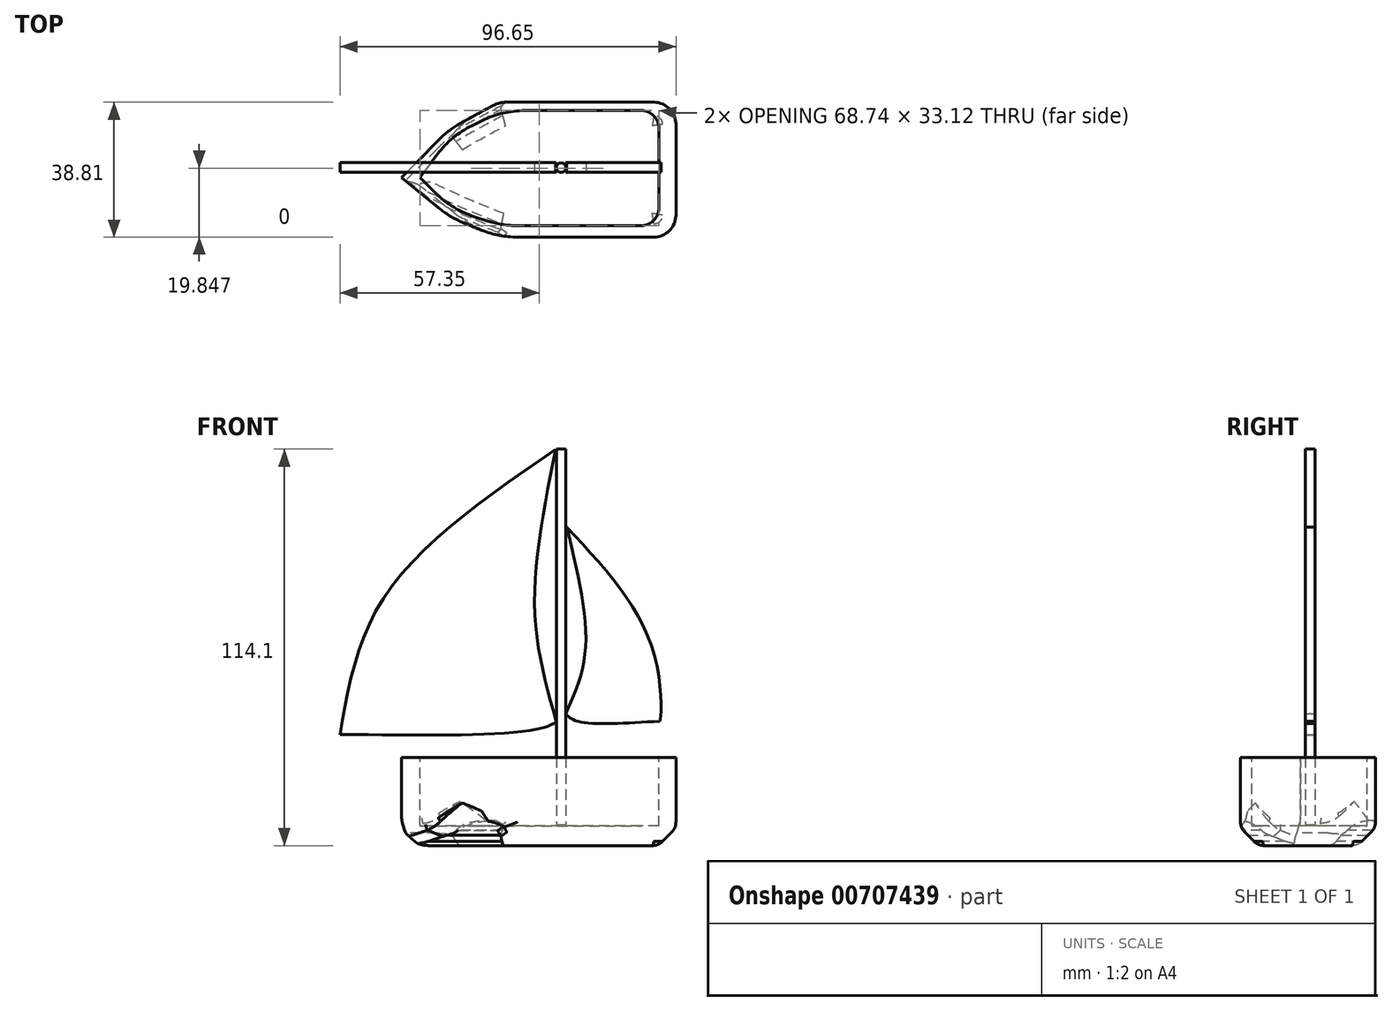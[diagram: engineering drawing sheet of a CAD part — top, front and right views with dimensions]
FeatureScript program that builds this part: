
annotation { "Feature Type Name" : "Feature", "Feature Type Description" : "" }
export const myFeature = defineFeature(function(context is Context, id is Id, definition is map)
    precondition{}
    {
        {
            var Q0;
            Q0=qCreatedBy(makeId("Top.planeOp"),FACE);
            var sketch = newSketch(context, id + "F0", { "sketchPlane" : qUnion([Q0])});
            skLineSegment(sketch, "E0", {"start": v(-20.58, 21.63) * mm, "end": v(23.87, 21.63) * mm});
            skLineSegment(sketch, "E1", {"start": v(-20.58, -17.18) * mm, "end": v(23.87, -17.18) * mm});
            skFitSpline(sketch, "E2", {"points": [v(-20.58, 21.63) * mm, v(-48.67, 0) * mm, v(-20.58, -17.18) * mm], "startDerivative": vector(-83.76, -44.37) * mm, "endDerivative": vector(84.8, -33.18) * mm});
            skLineSegment(sketch, "E3", {"start": v(-35.15, -11.18) * mm, "end": v(-48.67, 0) * mm});
            skLineSegment(sketch, "E4", {"start": v(-35.48, 13.4) * mm, "end": v(-48.67, 0) * mm});
            skLineSegment(sketch, "E5", {"start": v(30.22, 15.28) * mm, "end": v(30.22, -10.83) * mm});
            skPoint(sketch, "E6.visualSharp", {"position": v(30.22, 21.63) * mm});
            skArc(sketch, "E6.filletArc", {"start": v(30.22, 15.28) * mm, "mid": v(28.36, 19.77) * mm, "end": v(23.87, 21.63) * mm});
            skPoint(sketch, "E7.visualSharp", {"position": v(30.22, -17.18) * mm});
            skArc(sketch, "E7.filletArc", {"start": v(23.87, -17.18) * mm, "mid": v(28.36, -15.32) * mm, "end": v(30.22, -10.83) * mm});
            skSolve(sketch);
        }
        {
            var Q0;
            Q0=makeQuery(id+"F0.imprint","IMPRINT",FACE,{"disambiguationData":[TD([[makeQuery(id+"F0.imprint","IMPRINT",EDGE,{"derivedFrom":sQuery(id+"F0.wireOp",EDGE,"E0")}),-1.0]])]});
            extrude(context, id + "F1", {"entities" : qUnion([Q0]), "depth" : 25.4 * mm, "offsetDistance" : 25.4 * mm});
        }
        {
            var Q0;
            Q0=makeQuery(id+"F1.opExtrude","CAP_EDGE",EDGE,{"disambiguationData":[OSD([sQuery(id+"F0.wireOp",EDGE,"E2")])],"isStart":true});
            var Q1;
            Q1=makeQuery(id+"F1.opExtrude","CAP_EDGE",EDGE,{"disambiguationData":[OSD([sQuery(id+"F0.wireOp",EDGE,"E1")])],"isStart":true});
            var Q2;
            Q2=makeQuery(id+"F1.opExtrude","CAP_EDGE",EDGE,{"disambiguationData":[OSD([sQuery(id+"F0.wireOp",EDGE,"E4")])],"isStart":true});
            chamfer(context, id + "F2", {"entities" : qUnion([Q0, Q1, Q2]), "width" : 5.08 * mm, "tangentPropagation" : true});
        }
        {
            var Q0;
            Q0=makeQuery(id+"F2.opChamfer","BLEND_EDGE",EDGE,{"blendedFrom":[makeQuery(id+"F1.opExtrude","CAP_EDGE",EDGE,{"disambiguationData":[OSD([sQuery(id+"F0.wireOp",EDGE,"E2")])],"isStart":true}),makeQuery(id+"F1.opExtrude","SWEPT_FACE",FACE,{"disambiguationData":[OSD([sQuery(id+"F0.wireOp",EDGE,"E3")])]})],"blendedInto":[makeQuery(id+"F1.opExtrude","SWEPT_FACE",FACE,{"disambiguationData":[OSD([sQuery(id+"F0.wireOp",EDGE,"E3")])]})]});
            var Q1;
            {var subQ0=sQuery(id+"F0.wireOp",EDGE,"E4");Q1=makeQuery(id+"F2.opChamfer","BLEND_EDGE",EDGE,{"blendedFrom":[makeQuery(id+"F1.opExtrude","CAP_EDGE",EDGE,{"disambiguationData":[OSD([subQ0])],"isStart":true}),makeQuery(id+"F1.opExtrude","SWEPT_FACE",FACE,{"disambiguationData":[OSD([subQ0])]})],"blendedInto":[makeQuery(id+"F1.opExtrude","SWEPT_FACE",FACE,{"disambiguationData":[OSD([subQ0])]})]});}
            var Q2;
            {var subQ0=sQuery(id+"F0.wireOp",EDGE,"E2");Q2=makeQuery(id+"F2.opChamfer","BLEND_EDGE",EDGE,{"blendedFrom":[makeQuery(id+"F1.opExtrude","CAP_EDGE",EDGE,{"disambiguationData":[OSD([subQ0])],"isStart":true}),makeQuery(id+"F1.opExtrude","SWEPT_FACE",FACE,{"disambiguationData":[OSD([subQ0])]})],"blendedInto":[makeQuery(id+"F1.opExtrude","SWEPT_FACE",FACE,{"disambiguationData":[OSD([subQ0])]})]});}
            var Q3;
            Q3=makeQuery(id+"F2.opChamfer","BLEND_EDGE",EDGE,{"blendedFrom":[makeQuery(id+"F1.opExtrude","CAP_EDGE",EDGE,{"disambiguationData":[OSD([sQuery(id+"F0.wireOp",EDGE,"E4")])],"isStart":true}),makeQuery(id+"F1.opExtrude","SWEPT_FACE",FACE,{"disambiguationData":[OSD([sQuery(id+"F0.wireOp",EDGE,"E2")])]})],"blendedInto":[makeQuery(id+"F1.opExtrude","SWEPT_FACE",FACE,{"disambiguationData":[OSD([sQuery(id+"F0.wireOp",EDGE,"E2")])]})]});
            chamfer(context, id + "F3", {"entities" : qUnion([Q0, Q1, Q2, Q3]), "width" : 5.08 * mm, "tangentPropagation" : true});
        }
        {
            var Q0;
            {var subQ0=sQuery(id+"F0.wireOp",EDGE,"E2");Q0=makeQuery(id+"F3.opChamfer","BLEND_EDGE",EDGE,{"blendedFrom":[makeQuery(id+"F2.opChamfer","BLEND_EDGE",EDGE,{"blendedFrom":[makeQuery(id+"F1.opExtrude","CAP_EDGE",EDGE,{"disambiguationData":[OSD([subQ0])],"isStart":true}),makeQuery(id+"F1.opExtrude","SWEPT_FACE",FACE,{"disambiguationData":[OSD([subQ0])]})],"blendedInto":[makeQuery(id+"F1.opExtrude","SWEPT_FACE",FACE,{"disambiguationData":[OSD([subQ0])]})]}),makeQuery(id+"F2.opChamfer","BLEND_FACE",FACE,{"disambiguationData":[OSD([subQ0])]})],"blendedInto":[makeQuery(id+"F2.opChamfer","BLEND_FACE",FACE,{"disambiguationData":[OSD([subQ0])]})]});}
            var Q1;
            {var subQ0=sQuery(id+"F0.wireOp",EDGE,"E2");Q1=makeQuery(id+"F3.opChamfer","BLEND_EDGE",EDGE,{"blendedFrom":[makeQuery(id+"F2.opChamfer","BLEND_EDGE",EDGE,{"blendedFrom":[makeQuery(id+"F1.opExtrude","CAP_EDGE",EDGE,{"disambiguationData":[OSD([subQ0])],"isStart":true}),makeQuery(id+"F1.opExtrude","SWEPT_FACE",FACE,{"disambiguationData":[OSD([subQ0])]})],"blendedInto":[makeQuery(id+"F1.opExtrude","SWEPT_FACE",FACE,{"disambiguationData":[OSD([subQ0])]})]}),makeQuery(id+"F2.opChamfer","BLEND_FACE",FACE,{"disambiguationData":[OSD([sQuery(id+"F0.wireOp",EDGE,"E1")])]})],"blendedInto":[makeQuery(id+"F2.opChamfer","BLEND_FACE",FACE,{"disambiguationData":[OSD([sQuery(id+"F0.wireOp",EDGE,"E1")])]})]});}
            var Q2;
            {var subQ0=sQuery(id+"F0.wireOp",EDGE,"E1");Q2=makeQuery(id+"F2.opChamfer","BLEND_EDGE",EDGE,{"blendedFrom":[makeQuery(id+"F1.opExtrude","CAP_EDGE",EDGE,{"disambiguationData":[OSD([subQ0])],"isStart":true}),makeQuery(id+"F1.opExtrude","SWEPT_FACE",FACE,{"disambiguationData":[OSD([subQ0])]})],"blendedInto":[makeQuery(id+"F1.opExtrude","SWEPT_FACE",FACE,{"disambiguationData":[OSD([subQ0])]})]});}
            var Q3;
            {var subQ0=sQuery(id+"F0.wireOp",EDGE,"E1");Q3=makeQuery(id+"F2.opChamfer","BLEND_EDGE",EDGE,{"blendedFrom":[makeQuery(id+"F1.opExtrude","CAP_EDGE",EDGE,{"disambiguationData":[OSD([subQ0])],"isStart":true}),makeQuery(id+"F1.opExtrude","CAP_FACE",FACE,{"disambiguationData":[OSD([sQuery(id+"F0.wireOp",EDGE,"E0"),subQ0,sQuery(id+"F0.wireOp",EDGE,"E2"),sQuery(id+"F0.wireOp",EDGE,"E3"),sQuery(id+"F0.wireOp",EDGE,"E4"),sQuery(id+"F0.wireOp",EDGE,"E2"),sQuery(id+"F0.wireOp",EDGE,"E5"),sQuery(id+"F0.wireOp",EDGE,"E6.filletArc"),sQuery(id+"F0.wireOp",EDGE,"E7.filletArc")])],"isStart":true})],"blendedInto":[makeQuery(id+"F1.opExtrude","CAP_FACE",FACE,{"disambiguationData":[OSD([sQuery(id+"F0.wireOp",EDGE,"E0"),subQ0,sQuery(id+"F0.wireOp",EDGE,"E2"),sQuery(id+"F0.wireOp",EDGE,"E3"),sQuery(id+"F0.wireOp",EDGE,"E4"),sQuery(id+"F0.wireOp",EDGE,"E2"),sQuery(id+"F0.wireOp",EDGE,"E5"),sQuery(id+"F0.wireOp",EDGE,"E6.filletArc"),sQuery(id+"F0.wireOp",EDGE,"E7.filletArc")])],"isStart":true})]});}
            var Q4;
            {var subQ0=sQuery(id+"F0.wireOp",EDGE,"E2");Q4=makeQuery(id+"F2.opChamfer","BLEND_EDGE",EDGE,{"blendedFrom":[makeQuery(id+"F1.opExtrude","CAP_EDGE",EDGE,{"disambiguationData":[OSD([subQ0])],"isStart":true}),makeQuery(id+"F1.opExtrude","CAP_FACE",FACE,{"disambiguationData":[OSD([sQuery(id+"F0.wireOp",EDGE,"E0"),sQuery(id+"F0.wireOp",EDGE,"E1"),sQuery(id+"F0.wireOp",EDGE,"E2"),sQuery(id+"F0.wireOp",EDGE,"E3"),sQuery(id+"F0.wireOp",EDGE,"E4"),subQ0,sQuery(id+"F0.wireOp",EDGE,"E5"),sQuery(id+"F0.wireOp",EDGE,"E6.filletArc"),sQuery(id+"F0.wireOp",EDGE,"E7.filletArc")])],"isStart":true})],"blendedInto":[makeQuery(id+"F1.opExtrude","CAP_FACE",FACE,{"disambiguationData":[OSD([sQuery(id+"F0.wireOp",EDGE,"E0"),sQuery(id+"F0.wireOp",EDGE,"E1"),sQuery(id+"F0.wireOp",EDGE,"E2"),sQuery(id+"F0.wireOp",EDGE,"E3"),sQuery(id+"F0.wireOp",EDGE,"E4"),subQ0,sQuery(id+"F0.wireOp",EDGE,"E5"),sQuery(id+"F0.wireOp",EDGE,"E6.filletArc"),sQuery(id+"F0.wireOp",EDGE,"E7.filletArc")])],"isStart":true})]});}
            var Q5;
            {var subQ0=sQuery(id+"F0.wireOp",EDGE,"E4");var subQ1=makeQuery(id+"F1.opExtrude","SWEPT_FACE",FACE,{"disambiguationData":[OSD([subQ0])]});Q5=makeQuery(id+"F3.opChamfer","BLEND_EDGE",EDGE,{"blendedFrom":[makeQuery(id+"F2.opChamfer","BLEND_EDGE",EDGE,{"blendedFrom":[makeQuery(id+"F1.opExtrude","CAP_EDGE",EDGE,{"disambiguationData":[OSD([subQ0])],"isStart":true}),subQ1],"blendedInto":[subQ1]}),subQ1],"blendedInto":[subQ1]});}
            var Q6;
            {var subQ0=makeQuery(id+"F1.opExtrude","SWEPT_FACE",FACE,{"disambiguationData":[OSD([sQuery(id+"F0.wireOp",EDGE,"E2")])]});Q6=makeQuery(id+"F3.opChamfer","BLEND_EDGE",EDGE,{"blendedFrom":[makeQuery(id+"F2.opChamfer","BLEND_EDGE",EDGE,{"blendedFrom":[makeQuery(id+"F1.opExtrude","CAP_EDGE",EDGE,{"disambiguationData":[OSD([sQuery(id+"F0.wireOp",EDGE,"E4")])],"isStart":true}),subQ0],"blendedInto":[subQ0]}),subQ0],"blendedInto":[subQ0]});}
            var Q7;
            {var subQ0=sQuery(id+"F0.wireOp",EDGE,"E4");Q7=makeQuery(id+"F2.opChamfer","BLEND_EDGE",EDGE,{"blendedFrom":[makeQuery(id+"F1.opExtrude","CAP_EDGE",EDGE,{"disambiguationData":[OSD([subQ0])],"isStart":true}),makeQuery(id+"F1.opExtrude","CAP_FACE",FACE,{"disambiguationData":[OSD([sQuery(id+"F0.wireOp",EDGE,"E0"),sQuery(id+"F0.wireOp",EDGE,"E1"),sQuery(id+"F0.wireOp",EDGE,"E2"),sQuery(id+"F0.wireOp",EDGE,"E3"),subQ0,sQuery(id+"F0.wireOp",EDGE,"E2"),sQuery(id+"F0.wireOp",EDGE,"E5"),sQuery(id+"F0.wireOp",EDGE,"E6.filletArc"),sQuery(id+"F0.wireOp",EDGE,"E7.filletArc")])],"isStart":true})],"blendedInto":[makeQuery(id+"F1.opExtrude","CAP_FACE",FACE,{"disambiguationData":[OSD([sQuery(id+"F0.wireOp",EDGE,"E0"),sQuery(id+"F0.wireOp",EDGE,"E1"),sQuery(id+"F0.wireOp",EDGE,"E2"),sQuery(id+"F0.wireOp",EDGE,"E3"),subQ0,sQuery(id+"F0.wireOp",EDGE,"E2"),sQuery(id+"F0.wireOp",EDGE,"E5"),sQuery(id+"F0.wireOp",EDGE,"E6.filletArc"),sQuery(id+"F0.wireOp",EDGE,"E7.filletArc")])],"isStart":true})]});}
            var Q8;
            {var subQ0=makeQuery(id+"F1.opExtrude","SWEPT_FACE",FACE,{"disambiguationData":[OSD([sQuery(id+"F0.wireOp",EDGE,"E3")])]});Q8=makeQuery(id+"F3.opChamfer","BLEND_EDGE",EDGE,{"disambiguationData":[OD(1.0)],"blendedFrom":[makeQuery(id+"F2.opChamfer","BLEND_EDGE",EDGE,{"blendedFrom":[makeQuery(id+"F1.opExtrude","CAP_EDGE",EDGE,{"disambiguationData":[OSD([sQuery(id+"F0.wireOp",EDGE,"E2")])],"isStart":true}),subQ0],"blendedInto":[subQ0]}),subQ0],"blendedInto":[subQ0]});}
            var Q9;
            {var subQ0=makeQuery(id+"F1.opExtrude","SWEPT_FACE",FACE,{"disambiguationData":[OSD([sQuery(id+"F0.wireOp",EDGE,"E3")])]});Q9=makeQuery(id+"F3.opChamfer","BLEND_EDGE",EDGE,{"disambiguationData":[OD(0.0)],"blendedFrom":[makeQuery(id+"F2.opChamfer","BLEND_EDGE",EDGE,{"blendedFrom":[makeQuery(id+"F1.opExtrude","CAP_EDGE",EDGE,{"disambiguationData":[OSD([sQuery(id+"F0.wireOp",EDGE,"E2")])],"isStart":true}),subQ0],"blendedInto":[subQ0]}),subQ0],"blendedInto":[subQ0]});}
            var Q10;
            {var subQ0=sQuery(id+"F0.wireOp",EDGE,"E4");var subQ1=makeQuery(id+"F1.opExtrude","CAP_EDGE",EDGE,{"disambiguationData":[OSD([subQ0])],"isStart":true});Q10=makeQuery(id+"F3.opChamfer","BLEND_EDGE",EDGE,{"blendedFrom":[makeQuery(id+"F2.opChamfer","BLEND_EDGE",EDGE,{"blendedFrom":[subQ1,makeQuery(id+"F1.opExtrude","SWEPT_FACE",FACE,{"disambiguationData":[OSD([sQuery(id+"F0.wireOp",EDGE,"E2")])]})],"blendedInto":[makeQuery(id+"F1.opExtrude","SWEPT_FACE",FACE,{"disambiguationData":[OSD([sQuery(id+"F0.wireOp",EDGE,"E2")])]})]}),makeQuery(id+"F2.opChamfer","BLEND_EDGE",EDGE,{"blendedFrom":[subQ1,makeQuery(id+"F1.opExtrude","SWEPT_FACE",FACE,{"disambiguationData":[OSD([subQ0])]})],"blendedInto":[makeQuery(id+"F1.opExtrude","SWEPT_FACE",FACE,{"disambiguationData":[OSD([subQ0])]})]})],"blendedInto":[]});}
            var Q11;
            {var subQ0=sQuery(id+"F0.wireOp",EDGE,"E2");var subQ1=makeQuery(id+"F1.opExtrude","CAP_EDGE",EDGE,{"disambiguationData":[OSD([subQ0])],"isStart":true});Q11=makeQuery(id+"F3.opChamfer","BLEND_EDGE",EDGE,{"blendedFrom":[makeQuery(id+"F2.opChamfer","BLEND_EDGE",EDGE,{"blendedFrom":[subQ1,makeQuery(id+"F1.opExtrude","SWEPT_FACE",FACE,{"disambiguationData":[OSD([sQuery(id+"F0.wireOp",EDGE,"E3")])]})],"blendedInto":[makeQuery(id+"F1.opExtrude","SWEPT_FACE",FACE,{"disambiguationData":[OSD([sQuery(id+"F0.wireOp",EDGE,"E3")])]})]}),makeQuery(id+"F2.opChamfer","BLEND_EDGE",EDGE,{"blendedFrom":[subQ1,makeQuery(id+"F1.opExtrude","SWEPT_FACE",FACE,{"disambiguationData":[OSD([subQ0])]})],"blendedInto":[makeQuery(id+"F1.opExtrude","SWEPT_FACE",FACE,{"disambiguationData":[OSD([subQ0])]})]})],"blendedInto":[]});}
            fillet(context, id + "F4", {"entities" : qUnion([Q0, Q1, Q2, Q3, Q4, Q5, Q6, Q7, Q8, Q9, Q10, Q11]), "radius" : 4.14 * mm, "tangentPropagation" : true, "allowEdgeOverflow" : false});
        }
        {
            var Q0;
            Q0=makeQuery(id+"F1.opExtrude","CAP_FACE",FACE,{"disambiguationData":[OSD([sQuery(id+"F0.wireOp",EDGE,"E0"),sQuery(id+"F0.wireOp",EDGE,"E1"),sQuery(id+"F0.wireOp",EDGE,"E2"),sQuery(id+"F0.wireOp",EDGE,"E3"),sQuery(id+"F0.wireOp",EDGE,"E4"),sQuery(id+"F0.wireOp",EDGE,"E2"),sQuery(id+"F0.wireOp",EDGE,"E5"),sQuery(id+"F0.wireOp",EDGE,"E6.filletArc"),sQuery(id+"F0.wireOp",EDGE,"E7.filletArc")])],"isStart":false});
            cPlane(context, id + "F5", {"entities" : qUnion([Q0]), "cplaneType" : CPlaneType.OFFSET, "offset" : 0.05 * mm, "width" : 152.4 * mm, "height" : 152.4 * mm});
        }
        {
            var Q0;
            Q0=qCreatedBy(id+"F5.planeOp",FACE);
            var sketch = newSketch(context, id + "F6", { "sketchPlane" : qUnion([Q0])});
            skLineSegment(sketch, "E8", {"start": v(-19.67, 19.22) * mm, "end": v(20.2, 19.22) * mm});
            skLineSegment(sketch, "E9", {"start": v(25.29, 14.14) * mm, "end": v(25.29, -8.81) * mm});
            skLineSegment(sketch, "E10", {"start": v(20.2, -13.9) * mm, "end": v(-19.67, -13.9) * mm});
            skPoint(sketch, "E11.visualSharp", {"position": v(25.29, 19.22) * mm});
            skArc(sketch, "E11.filletArc", {"start": v(25.29, 14.14) * mm, "mid": v(23.8, 17.74) * mm, "end": v(20.2, 19.22) * mm});
            skPoint(sketch, "E12.visualSharp", {"position": v(25.29, -13.9) * mm});
            skArc(sketch, "E12.filletArc", {"start": v(20.2, -13.9) * mm, "mid": v(23.8, -12.4) * mm, "end": v(25.29, -8.81) * mm});
            skLineSegment(sketch, "E13", {"start": v(-19.67, 19.22) * mm, "end": v(-34.35, 11.98) * mm});
            skLineSegment(sketch, "E14", {"start": v(-34.35, 11.98) * mm, "end": v(-43.45, 0) * mm});
            skLineSegment(sketch, "E15", {"start": v(-43.45, 0) * mm, "end": v(-34.07, -9.28) * mm});
            skLineSegment(sketch, "E16", {"start": v(-34.07, -9.28) * mm, "end": v(-19.67, -13.9) * mm});
            skSolve(sketch);
        }
        {
            var Q0;
            Q0=makeQuery(id+"F6.imprint","IMPRINT",FACE,{"disambiguationData":[TD([[makeQuery(id+"F6.imprint","IMPRINT",EDGE,{"derivedFrom":sQuery(id+"F6.wireOp",EDGE,"aaz5tSlX-TM4P-ws5N-pEF1-roB0Ln3QjQEB")}),-1.0]])]});
            var Q1;
            Q1=makeQuery(id+"F6.imprint","IMPRINT",FACE,{"disambiguationData":[TD([[makeQuery(id+"F6.imprint","IMPRINT",EDGE,{"derivedFrom":sQuery(id+"F6.wireOp",EDGE,"E8")}),-1.0]])]});
            extrude(context, id + "F7", {"entities" : qUnion([Q0, Q1]), "operationType" : NewBodyOperationType.REMOVE, "oppositeDirection" : true, "depth" : 19.8 * mm, "offsetDistance" : 25.4 * mm});
        }
        {
            var Q0;
            Q0=makeQuery(id+"F7.boolean.opBoolean","COPY",EDGE,{"derivedFrom":makeQuery(id+"F7.opExtrude","SWEPT_EDGE",EDGE,{"disambiguationData":[OSD([sQuery(id+"F6.wireOp",EDGE,"E8"),sQuery(id+"F6.wireOp",EDGE,"E13")])]})});
            var Q1;
            Q1=makeQuery(id+"F7.boolean.opBoolean","COPY",EDGE,{"derivedFrom":makeQuery(id+"F7.opExtrude","SWEPT_EDGE",EDGE,{"disambiguationData":[OSD([sQuery(id+"F6.wireOp",EDGE,"E13"),sQuery(id+"F6.wireOp",EDGE,"E14")])]})});
            var Q2;
            Q2=makeQuery(id+"F7.boolean.opBoolean","COPY",EDGE,{"derivedFrom":makeQuery(id+"F7.opExtrude","SWEPT_EDGE",EDGE,{"disambiguationData":[OSD([sQuery(id+"F6.wireOp",EDGE,"E10"),sQuery(id+"F6.wireOp",EDGE,"E16")])]})});
            var Q3;
            Q3=makeQuery(id+"F7.boolean.opBoolean","COPY",EDGE,{"derivedFrom":makeQuery(id+"F7.opExtrude","SWEPT_EDGE",EDGE,{"disambiguationData":[OSD([sQuery(id+"F6.wireOp",EDGE,"E15"),sQuery(id+"F6.wireOp",EDGE,"E16")])]})});
            var Q4;
            Q4=makeQuery(id+"F1.opExtrude","SWEPT_EDGE",EDGE,{"disambiguationData":[OSD([sQuery(id+"F0.wireOp",EDGE,"E3"),sQuery(id+"F0.wireOp",EDGE,"E2")])]});
            var Q5;
            Q5=makeQuery(id+"F1.opExtrude","SWEPT_EDGE",EDGE,{"disambiguationData":[OSD([sQuery(id+"F0.wireOp",EDGE,"E1"),sQuery(id+"F0.wireOp",EDGE,"E2")])]});
            var Q6;
            Q6=makeQuery(id+"F1.opExtrude","SWEPT_EDGE",EDGE,{"disambiguationData":[OSD([sQuery(id+"F0.wireOp",EDGE,"E2"),sQuery(id+"F0.wireOp",EDGE,"E4")])]});
            fillet(context, id + "F8", {"entities" : qUnion([Q0, Q1, Q2, Q3, Q4, Q5, Q6]), "radius" : 27.76 * mm, "tangentPropagation" : true, "allowEdgeOverflow" : false});
        }
        {
            var Q0;
            Q0=makeQuery(id+"F1.opExtrude","SWEPT_EDGE",EDGE,{"disambiguationData":[OSD([sQuery(id+"F0.wireOp",EDGE,"E0"),sQuery(id+"F0.wireOp",EDGE,"E2")])]});
            fillet(context, id + "F9", {"entities" : qUnion([Q0]), "radius" : 7.62 * mm, "tangentPropagation" : true, "allowEdgeOverflow" : false});
        }
        {
            var Q0;
            Q0=makeQuery(id+"F7.boolean.opBoolean","COPY",FACE,{"derivedFrom":makeQuery(id+"F7.opExtrude","CAP_FACE",FACE,{"disambiguationData":[OSD([sQuery(id+"F6.wireOp",EDGE,"E8"),sQuery(id+"F6.wireOp",EDGE,"E9"),sQuery(id+"F6.wireOp",EDGE,"E10"),sQuery(id+"F6.wireOp",EDGE,"E11.filletArc"),sQuery(id+"F6.wireOp",EDGE,"E12.filletArc"),sQuery(id+"F6.wireOp",EDGE,"E13"),sQuery(id+"F6.wireOp",EDGE,"E14"),sQuery(id+"F6.wireOp",EDGE,"E15"),sQuery(id+"F6.wireOp",EDGE,"E16")])],"isStart":false})});
            var Q1;
            Q1 = qBodyType(qCreatedBy(id + "F11" ,EDGE), BodyType.WIRE);
            cPlane(context, id + "F10", {"entities" : qUnion([Q0, Q1]), "cplaneType" : CPlaneType.OFFSET, "offset" : 0.25 * mm, "width" : 152.4 * mm, "height" : 152.4 * mm});
        }
        {
            var Q0;
            Q0=qCreatedBy(id+"F10.planeOp",FACE);
            var sketch = newSketch(context, id + "F11", { "sketchPlane" : qUnion([Q0])});
            skCircle(sketch, "E17", {"center": v(-2.8, 2.83) * mm, "radius": 1.37 * mm});
            skSolve(sketch);
        }
        {
            var Q0;
            Q0=makeQuery(id+"F11.imprint","IMPRINT",FACE,{"disambiguationData":[TD([[makeQuery(id+"F11.imprint","IMPRINT",EDGE,{"derivedFrom":sQuery(id+"F11.wireOp",EDGE,"E17")}),1.0]])]});
            extrude(context, id + "F12", {"entities" : qUnion([Q0]), "depth" : 108.2 * mm, "offsetDistance" : 25.4 * mm});
        }
        {
            var Q0;
            Q0=qCreatedBy(makeId("Front.planeOp"),FACE);
            cPlane(context, id + "F13", {"entities" : qUnion([Q0]), "cplaneType" : CPlaneType.OFFSET, "offset" : 4.3 * mm, "oppositeDirection" : true, "width" : 152.4 * mm, "height" : 152.4 * mm});
        }
        {
            var Q0;
            Q0=qCreatedBy(id+"F13.planeOp",FACE);
            var sketch = newSketch(context, id + "F14", { "sketchPlane" : qUnion([Q0])});
            skFitSpline(sketch, "E18", {"points": [v(-4.36, 114.02) * mm, v(-53.31, 72.06) * mm, v(-66.43, 32.02) * mm], "startDerivative": vector(-104.88, -72.09) * mm, "endDerivative": vector(-16.1, -92.62) * mm});
            skFitSpline(sketch, "E19", {"points": [v(-66.43, 32.02) * mm, v(-8.28, 33.82) * mm, v(-4.21, 35.82) * mm, v(-4.27, 36.05) * mm], "startDerivative": vector(98.6, -1.34) * mm, "endDerivative": vector(-2.63, 4.33) * mm});
            skFitSpline(sketch, "E20", {"points": [v(-4.36, 114.02) * mm, v(-10.42, 68.46) * mm, v(-4.21, 35.82) * mm], "startDerivative": vector(-17.87, -87.88) * mm, "endDerivative": vector(19.18, -67.98) * mm});
            skFitSpline(sketch, "E21", {"points": [v(-1.19, 91.7) * mm, v(23.95, 55.11) * mm, v(25.62, 35.82) * mm, v(25.57, 35.82) * mm], "startDerivative": vector(54.3, -58.4) * mm, "endDerivative": vector(-2.64, 1.32) * mm});
            skFitSpline(sketch, "E22", {"points": [v(25.62, 35.82) * mm, v(1.78, 35.82) * mm, v(-1.46, 37.9) * mm], "startDerivative": vector(-41.32, -2.6) * mm, "endDerivative": vector(-8.12, 8.32) * mm});
            skFitSpline(sketch, "E23", {"points": [v(-1.19, 91.7) * mm, v(4.22, 56.99) * mm, v(-1.46, 37.9) * mm], "startDerivative": vector(15.96, -65.54) * mm, "endDerivative": vector(-18.1, -40.9) * mm});
            skSolve(sketch);
        }
        {
            var Q0;
            {var subQ0=sQuery(id+"F14.wireOp",EDGE,"E18");Q0=makeQuery(id+"F14.imprint","IMPRINT",FACE,{"disambiguationData":[TD([[makeQuery(id+"F14.imprint","IMPRINT",EDGE,{"derivedFrom":subQ0}),1.0]])]});}
            var Q1;
            {var subQ0=sQuery(id+"F14.wireOp",EDGE,"E23");Q1=makeQuery(id+"F14.imprint","IMPRINT",FACE,{"disambiguationData":[TD([[makeQuery(id+"F14.imprint","IMPRINT",EDGE,{"derivedFrom":subQ0}),1.0]])]});}
            extrude(context, id + "F15", {"entities" : qUnion([Q0, Q1]), "operationType" : NewBodyOperationType.ADD, "depth" : 2.8 * mm, "offsetDistance" : 25.4 * mm});
        }
    });
